# Revit family: 0044183 Feilo Sylvania Lighting Fixture OPTIX R 1200 1L 3K ALU
name_source: partatom
category: Lighting Fixtures
revit_build: Autodesk Revit 2017 (Build: 20190507_1515(x64)
units: mm (PartAtom-declared; Revit-internal decimal feet)

## family parameters
Cut with Voids When Loaded = No
Host = Face
Light Source = Yes
OmniClass Number = 23.80.70.00
OmniClass Title = Lighting
Part Type = Normal
Room Calculation Point = No
Round Connector Dimension = Use Diameter
Shared = No

## types (1)
- 0044183 OPTIX R 1200 1L 3K ALU
    Apparent Load = 26 VA
    Assembly Code = D5020200
    AssetType = Fixed
    ClassificationName = Uniclass2015
    ClassificationValue = EF_70_80
    Color Filter = 16777215
    Cost = 0 $
    Default Elevation = 1219 mm
    Description = OPTIX RECESSED 1200X300 1L 3000K ALU is a high efficacy low glare luminaire for office and education applications. Ceiling recessed 1200x300 mm. Aluminised plastic extra low glare optics in 1 line configuration. White RAL9016 fixture body. Constant current driver. 3000K Warm White LED, CRI>80, chromaticity tolerance of 3-step MacAdam ellipse. Luminous flux 3200lm. Power consumption 26W. Luminaire efficacy 123lm/W. Lumen maintenance of L90B50 > 72000h, L90B10 = 46000h. UGR<16, IK07, IP20. Photobiological safety risk group 1. Electrical protection Class I. Glow wire test 650°C.
    Dimming Lamp Color Temperature Shift = <None>
    DocumentationLiterature = http://www.sylvania-lighting.com
    DurationUnit = hours
    ElectricShockClassification = Class I
    Emit Shape Visible in Rendering = No
    Emit from Circle Diameter = 610 mm
    ExpectedLife = 50000
    Height = 38 mm  [stored 0.124672 ft]
    IfcExportAs = IfcLightFixtureType
    IfcExportType = IfcLightFixtureType
    ImpactProtectionIndex = IK07
    IngressProtection = IP20
    InputNominalFrequency = 50/60 Hz
    InputVoltage = 220-240V~
    Keynote = 16500
    Lamp = LED
    LampColourRenderingIndex = 80
    LampColourTemperature = 3000 K
    LampMacAdamStep = 3
    LampNominalLuminous = 3200 lm
    LampsType = LED
    Length = 1196 mm  [stored 3.92388 ft]
    LuminousEfficacy = 123 lm/W
    Manufacturer = Feilo Sylvania
    ManufacturerName = Feilo Sylvania
    Material = steel housing, polycarbonate diffuser
    Material_1_FEILO = <By Category>
    Material_2_FEILO = <By Category>
    Material_3_FEILO = <By Category>
    Material_4_FEILO = <By Category>
    Model = OPTIX R 1200 1L 3K ALU
    ModelNumber = 0044183
    ModelReference = OPTIX R 1200 1L 3K ALU
    Name = OPTIX R 1200 1L 3K ALU
    NominalDepth = 296 mm  [stored 0.971129 ft]
    NominalHeight = 38 mm  [stored 0.124672 ft]
    NominalLength = 1196 mm  [stored 3.92388 ft]
    Photometric Web File = 0044183.ies
    PowerConsumption = 26 W
    PowerFactor = 0.95
    Tilt Angle = 90.00°
    Type Image = <None>
    TypeName = OPTIX R 1200 1L 3K ALU
    URL = http://www.sylvania-lighting.com
    Voltage = 230 V
    Weight = 5.0 kg
    Width = 296 mm  [stored 0.971129 ft]

note: [stored X ft] marks values corroborated as IEEE doubles in the binary element streams (Revit-internal decimal feet)

## geometry (parser evidence)
native form markers: Sweep x2
no freeform markers — native parametric forms only
